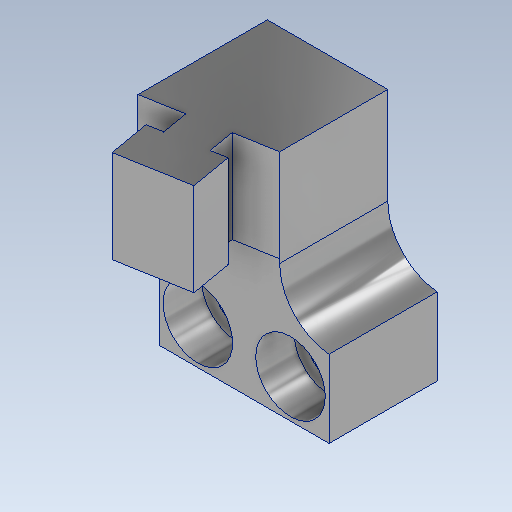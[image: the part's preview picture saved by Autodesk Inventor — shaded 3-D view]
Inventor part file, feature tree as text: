
AUTODESK INVENTOR PART (.ipt)
format: ipt  version: 2025.2 (Build 292293000, 293)  size: 217,088 bytes
history: native  units: mm
features: extrude x4, sketch x4, fillet x1
ambient origin geometry x8: Origin, YZ Plane, XZ Plane, XY Plane, X Axis, Y Axis, Z Axis, Center Point
bodies: Solid2 (feature_tree)
feature tree (9):
  extrude  "Extrusion2"  Depth=15.6mm
  extrude  "Extrusion9"  Depth=29.5mm
  extrude  "Extrusion10"  Depth=10.0mm
  fillet  "Rundung3"  Radius=12.526mm
  extrude  "Extrusion11"  Depth=5.0mm
  sketch  "Sketch5"  dims[d56=14.0mm d57=0.0mm d67=15.6mm]
  sketch  "Skizze14"  dims[d111=15.6mm d112=29.5mm]
  sketch  "Skizze16"  dims[d113=22.0mm d114=10.0mm d116=12.526mm]
  sketch  "Skizze17"  dims[d117=5.0mm d118=5.0mm d119=12.0mm d120=5.0mm d121=9.0mm d122=9.0mm d123=5.5mm d124=5.5mm d125=5.0mm d126=0.0mm d127=5.0mm d128=5.0mm d129=5.0mm d130=5.0mm d131=5.5mm d132=5.5mm d133=15.0mm d134=0.0mm d135=7.0mm d136=2.751mm d137=13.962634mm d141=3.5mm d143=2.0mm d144=5.4mm d145=9.15mm d147=2.0mm d150=12.0mm d151=0.0mm]
